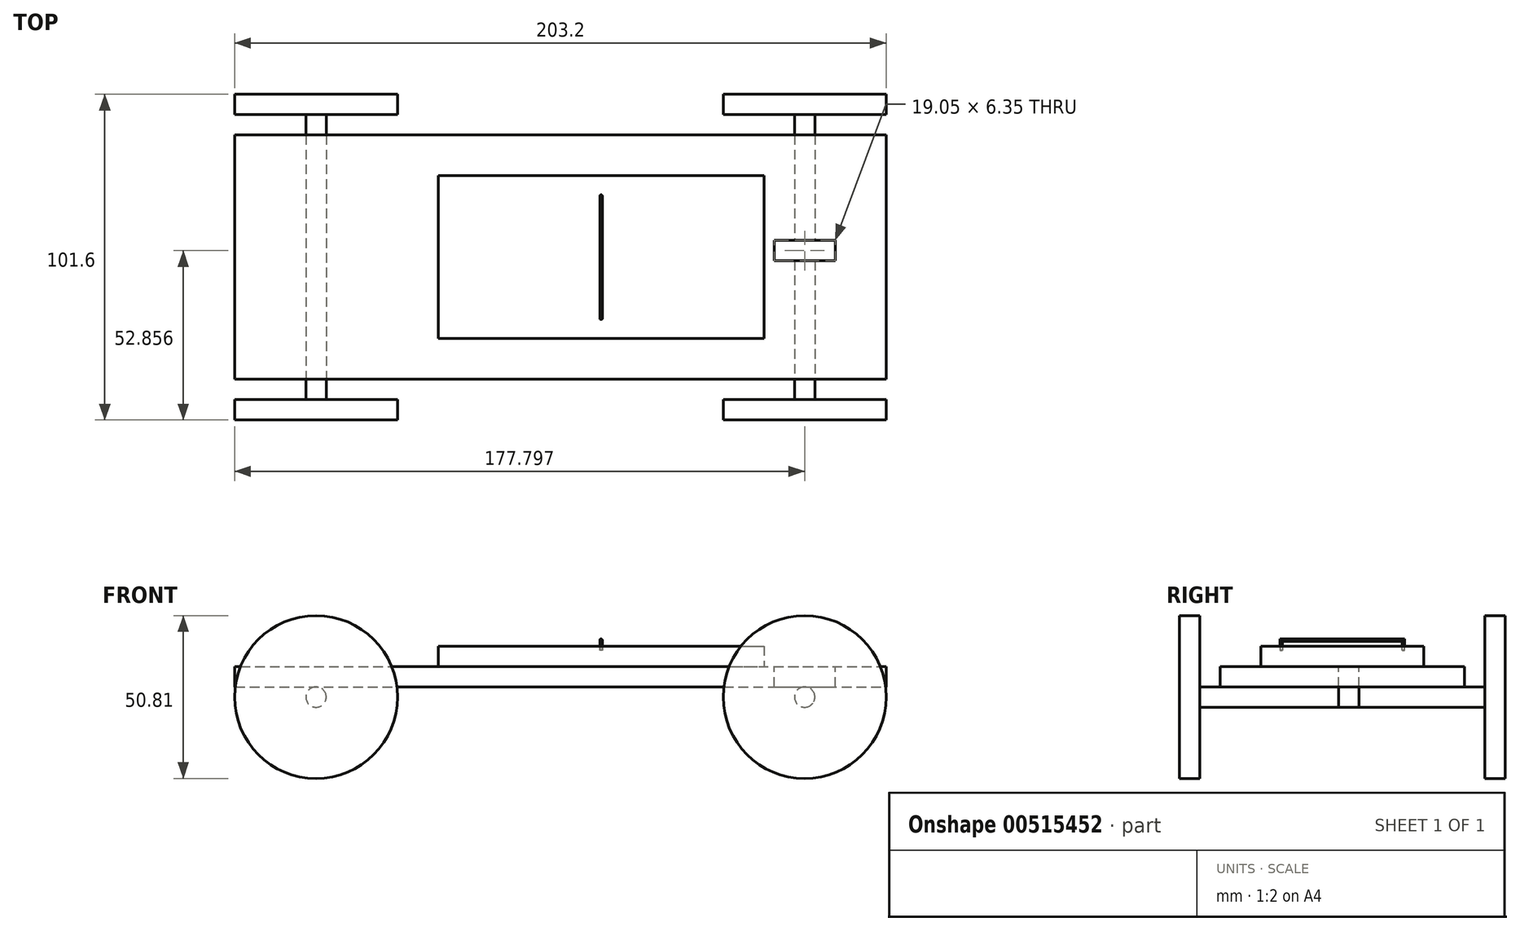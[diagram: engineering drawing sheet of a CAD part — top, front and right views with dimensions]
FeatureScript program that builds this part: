
annotation { "Feature Type Name" : "Feature", "Feature Type Description" : "" }
export const myFeature = defineFeature(function(context is Context, id is Id, definition is map)
    precondition{}
    {
        {
            var Q0;
            Q0=qCreatedBy(makeId("Top.planeOp"),FACE);
            var sketch = newSketch(context, id + "F0", { "sketchPlane" : qUnion([Q0])});
            skLineSegment(sketch, "E0.bottom", {"start": v(-129.01, -39.77) * mm, "end": v(74.19, -39.77) * mm});
            skLineSegment(sketch, "E0.top", {"start": v(-129.01, 36.43) * mm, "end": v(74.19, 36.43) * mm});
            skLineSegment(sketch, "E0.left", {"start": v(-129.01, -39.77) * mm, "end": v(-129.01, 36.43) * mm});
            skLineSegment(sketch, "E0.right", {"start": v(74.19, -39.77) * mm, "end": v(74.19, 36.43) * mm});
            skSolve(sketch);
        }
        {
            var Q0;
            Q0 = qSketchRegion(id + "F0", true);
            extrude(context, id + "F1", {"entities" : qUnion([Q0]), "depth" : 6.35 * mm, "offsetDistance" : 25.4 * mm});
        }
        {
            var Q0;
            Q0=makeQuery(id+"F1.opExtrude","SWEPT_FACE",FACE,{"disambiguationData":[OSD([sQuery(id+"F0.wireOp",EDGE,"E0.bottom")])]});
            var sketch = newSketch(context, id + "F2", { "sketchPlane" : qUnion([Q0])});
            skCircle(sketch, "E1", {"center": v(48.79, -3.17) * mm, "radius": 3.18 * mm});
            skSolve(sketch);
        }
        {
            var Q0;
            Q0=makeQuery(id+"F2.imprint","IMPRINT",FACE,{"disambiguationData":[TD([[makeQuery(id+"F2.imprint","IMPRINT",EDGE,{"derivedFrom":sQuery(id+"F2.wireOp",EDGE,"E1")}),1.0]])]});
            extrude(context, id + "F3", {"entities" : qUnion([Q0]), "operationType" : NewBodyOperationType.ADD, "depth" : -82.55 * mm, "offsetDistance" : 25.4 * mm});
        }
        {
            var Q0;
            Q0=makeQuery(id+"F3.opExtrude","CAP_FACE",FACE,{"disambiguationData":[OSD([sQuery(id+"F2.wireOp",EDGE,"E1")])],"isStart":true});
            extrude(context, id + "F4", {"entities" : qUnion([Q0]), "operationType" : NewBodyOperationType.ADD, "depth" : 6.35 * mm, "offsetDistance" : 25.4 * mm});
        }
        {
            var Q0;
            Q0=makeQuery(id+"F3.opExtrude","CAP_FACE",FACE,{"disambiguationData":[OSD([sQuery(id+"F2.wireOp",EDGE,"E1")])],"isStart":false});
            var sketch = newSketch(context, id + "F5", { "sketchPlane" : qUnion([Q0])});
            skCircle(sketch, "E2", {"center": v(-48.79, -3.17) * mm, "radius": 25.4 * mm});
            skSolve(sketch);
        }
        {
            var Q0;
            Q0 = qSketchRegion(id + "F5", true);
            extrude(context, id + "F6", {"entities" : qUnion([Q0]), "operationType" : NewBodyOperationType.ADD, "depth" : 6.35 * mm, "offsetDistance" : 25.4 * mm});
        }
        {
            var Q0;
            Q0=makeQuery(id+"F4.opExtrude","CAP_FACE",FACE,{"disambiguationData":[OSD([sQuery(id+"F2.wireOp",EDGE,"E1")])],"isStart":false});
            var sketch = newSketch(context, id + "F7", { "sketchPlane" : qUnion([Q0])});
            skCircle(sketch, "E3", {"center": v(48.79, -3.17) * mm, "radius": 25.4 * mm});
            skSolve(sketch);
        }
        {
            var Q0;
            Q0=makeQuery(id+"F7.imprint","IMPRINT",FACE,{"disambiguationData":[TD([[makeQuery(id+"F7.imprint","IMPRINT",EDGE,{"derivedFrom":makeQuery(id+"F4.opExtrude","CAP_EDGE",EDGE,{"disambiguationData":[OSD([sQuery(id+"F2.wireOp",EDGE,"E1")])],"isStart":false})}),1.0]])]});
            var Q1;
            Q1=makeQuery(id+"F7.imprint","IMPRINT",FACE,{"disambiguationData":[TD([[makeQuery(id+"F7.imprint","IMPRINT",EDGE,{"derivedFrom":sQuery(id+"F7.wireOp",EDGE,"E3")}),1.0]])]});
            extrude(context, id + "F8", {"entities" : qUnion([Q0, Q1]), "operationType" : NewBodyOperationType.ADD, "depth" : 6.35 * mm, "offsetDistance" : 25.4 * mm});
        }
        {
            var Q0;
            Q0=makeQuery(id+"F1.opExtrude","SWEPT_FACE",FACE,{"disambiguationData":[OSD([sQuery(id+"F0.wireOp",EDGE,"E0.right")])]});
            cPlane(context, id + "F9", {"entities" : qUnion([Q0]), "cplaneType" : CPlaneType.OFFSET, "offset" : 101.6 * mm, "oppositeDirection" : true, "width" : 152.4 * mm, "height" : 152.4 * mm});
        }
        {
            var Q0;
            Q0=makeQuery(id+"F3.opExtrude","SWEPT_BODY",BODY,{"disambiguationData":[OSD([sQuery(id+"F2.wireOp",EDGE,"E1")])]});
            var Q1;
            Q1=qCreatedBy(id+"F9.planeOp",FACE);
            mirror(context, id + "F10", {"operationType" : NewBodyOperationType.ADD, "entities" : qUnion([Q0]), "mirrorPlane" : qUnion([Q1])});
        }
        {
            var Q0;
            Q0=makeQuery(id+"F1.opExtrude","CAP_FACE",FACE,{"disambiguationData":[OSD([sQuery(id+"F0.wireOp",EDGE,"E0.bottom"),sQuery(id+"F0.wireOp",EDGE,"E0.top"),sQuery(id+"F0.wireOp",EDGE,"E0.left"),sQuery(id+"F0.wireOp",EDGE,"E0.right")])],"isStart":false});
            var sketch = newSketch(context, id + "F11", { "sketchPlane" : qUnion([Q0])});
            skLineSegment(sketch, "E4.bottom", {"start": v(-65.51, 23.73) * mm, "end": v(36.09, 23.73) * mm});
            skLineSegment(sketch, "E4.top", {"start": v(-65.51, -27.07) * mm, "end": v(36.09, -27.07) * mm});
            skLineSegment(sketch, "E4.left", {"start": v(-65.51, 23.73) * mm, "end": v(-65.51, -27.07) * mm});
            skLineSegment(sketch, "E4.right", {"start": v(36.09, 23.73) * mm, "end": v(36.09, -27.07) * mm});
            skSolve(sketch);
        }
        {
            var Q0;
            Q0=makeQuery(id+"F11.imprint","IMPRINT",FACE,{"disambiguationData":[TD([[makeQuery(id+"F11.imprint","IMPRINT",EDGE,{"derivedFrom":sQuery(id+"F11.wireOp",EDGE,"E4.bottom")}),-1.0]])]});
            extrude(context, id + "F12", {"entities" : qUnion([Q0]), "operationType" : NewBodyOperationType.ADD, "depth" : 6.35 * mm, "offsetDistance" : 25.4 * mm});
        }
        {
            var Q0;
            Q0=makeQuery(id+"F1.opExtrude","CAP_FACE",FACE,{"disambiguationData":[OSD([sQuery(id+"F0.wireOp",EDGE,"E0.bottom"),sQuery(id+"F0.wireOp",EDGE,"E0.top"),sQuery(id+"F0.wireOp",EDGE,"E0.left"),sQuery(id+"F0.wireOp",EDGE,"E0.right")])],"isStart":false});
            var sketch = newSketch(context, id + "F13", { "sketchPlane" : qUnion([Q0])});
            skLineSegment(sketch, "E5.bottom", {"start": v(39.26, 3.56) * mm, "end": v(58.31, 3.56) * mm});
            skLineSegment(sketch, "E5.top", {"start": v(39.26, -2.79) * mm, "end": v(58.31, -2.79) * mm});
            skLineSegment(sketch, "E5.left", {"start": v(39.26, 3.56) * mm, "end": v(39.26, -2.79) * mm});
            skLineSegment(sketch, "E5.right", {"start": v(58.31, 3.56) * mm, "end": v(58.31, -2.79) * mm});
            skPoint(sketch, "E6", {"position": v(48.79, 0.39) * mm});
            skPoint(sketch, "E6.positionSnap0", {"position": v(58.31, 0.39) * mm});
            skPoint(sketch, "E6.positionSnap1", {"position": v(48.79, 3.56) * mm});
            skSolve(sketch);
        }
        {
            var Q0;
            Q0=makeQuery(id+"F13.imprint","IMPRINT",FACE,{"disambiguationData":[TD([[makeQuery(id+"F13.imprint","IMPRINT",EDGE,{"derivedFrom":sQuery(id+"F13.wireOp",EDGE,"E5.bottom")}),-1.0]])]});
            extrude(context, id + "F14", {"entities" : qUnion([Q0]), "operationType" : NewBodyOperationType.REMOVE, "oppositeDirection" : true, "depth" : 25.4 * mm, "offsetDistance" : 25.4 * mm});
        }
        {
            var Q0;
            Q0=makeQuery(id+"F12.opExtrude","CAP_FACE",FACE,{"disambiguationData":[OSD([sQuery(id+"F11.wireOp",EDGE,"E4.bottom"),sQuery(id+"F11.wireOp",EDGE,"E4.top"),sQuery(id+"F11.wireOp",EDGE,"E4.left"),sQuery(id+"F11.wireOp",EDGE,"E4.right")])],"isStart":false});
            var sketch = newSketch(context, id + "F15", { "sketchPlane" : qUnion([Q0])});
            skCircle(sketch, "E7", {"center": v(5.35, 16.55) * mm, "radius": 0.4 * mm});
            skSolve(sketch);
        }
        {
            var Q0;
            Q0=qCreatedBy(id+"F9.planeOp",FACE);
            cPlane(context, id + "F16", {"entities" : qUnion([Q0]), "cplaneType" : CPlaneType.OFFSET, "offset" : 12.7 * mm, "width" : 152.4 * mm, "height" : 152.4 * mm});
        }
        {
            var Q0;
            Q0=qCreatedBy(id+"F16.planeOp",FACE);
            var sketch = newSketch(context, id + "F17", { "sketchPlane" : qUnion([Q0])});
            skLineSegment(sketch, "E8", {"start": v(17.38, 11.35) * mm, "end": v(17.38, 14.53) * mm});
            skLineSegment(sketch, "E9", {"start": v(-20.72, 14.53) * mm, "end": v(-20.72, 11.35) * mm});
            skLineSegment(sketch, "E10", {"start": v(-20.72, 14.53) * mm, "end": v(17.38, 14.53) * mm});
            skSolve(sketch);
        }
        {
            var Q0;
            Q0=makeQuery(id+"F15.imprint","IMPRINT",FACE,{"disambiguationData":[TD([[makeQuery(id+"F15.imprint","IMPRINT",EDGE,{"derivedFrom":sQuery(id+"F15.wireOp",EDGE,"E7")}),-1.0]])]});
            var sketch = newSketch(context, id + "F18", { "sketchPlane" : qUnion([Q0])});
            skCircle(sketch, "E11", {"center": v(-14.71, 17.38) * mm, "radius": 0.4 * mm});
            skSolve(sketch);
        }
        {
            var Q0;
            Q0=makeQuery(id+"F18.imprint","IMPRINT",FACE,{"disambiguationData":[TD([[makeQuery(id+"F18.imprint","IMPRINT",EDGE,{"derivedFrom":sQuery(id+"F18.wireOp",EDGE,"E11")}),1.0]])]});
            var Q1;
            Q1 = qConstructionFilter(qBodyType(qCreatedBy(id + "F17" ,EDGE), BodyType.WIRE), ConstructionObject.NO);
            sweep(context, id + "F19", {"profiles" : qUnion([Q0]), "path" : qUnion([Q1])});
        }
    });
